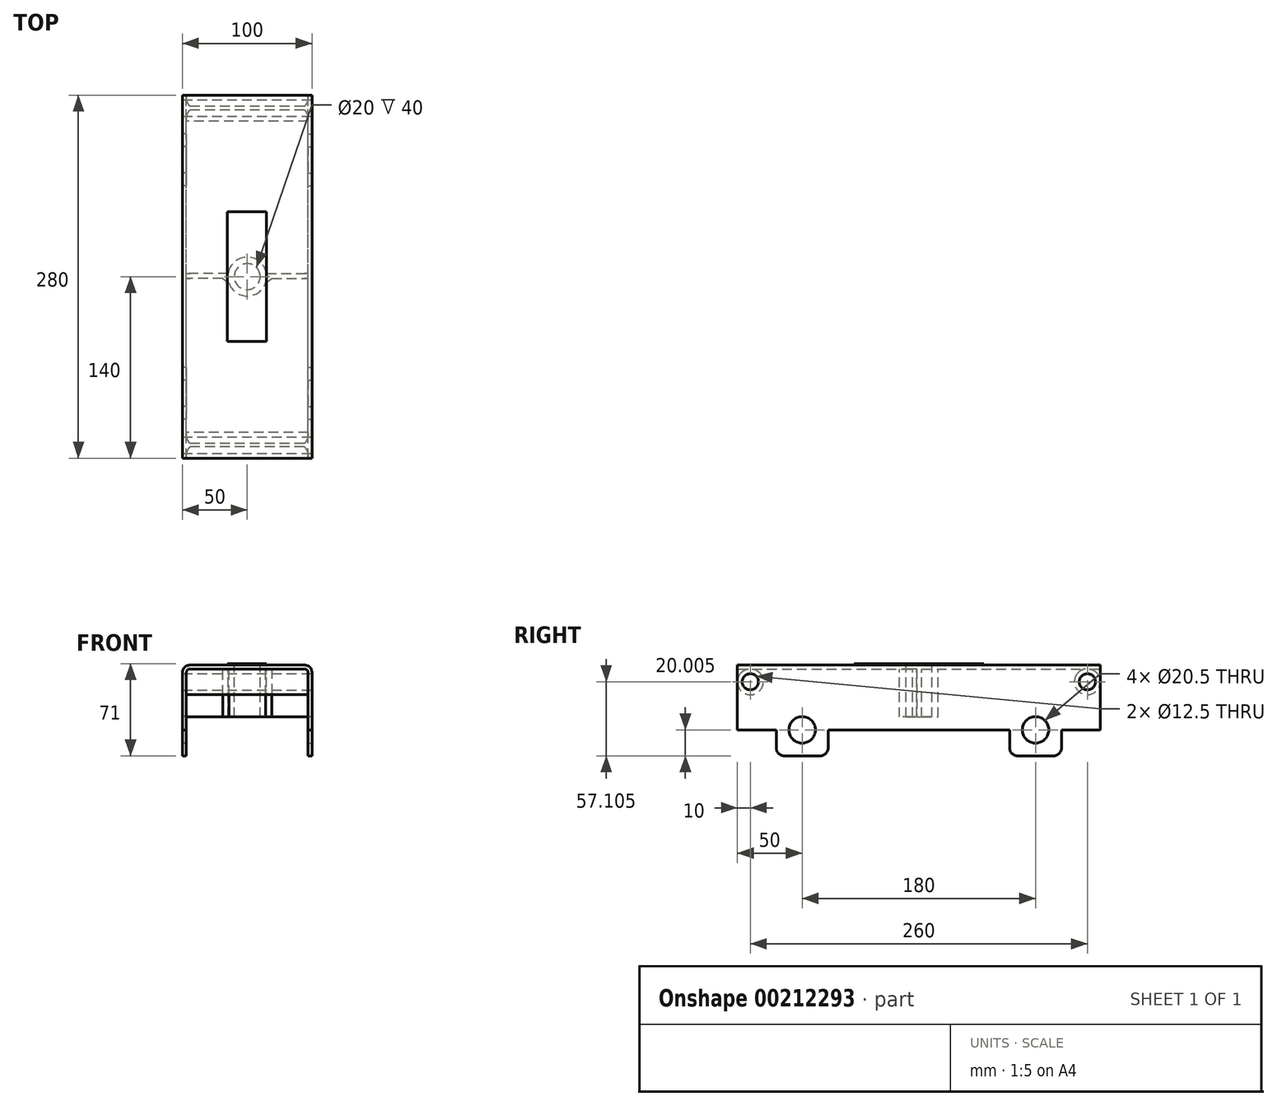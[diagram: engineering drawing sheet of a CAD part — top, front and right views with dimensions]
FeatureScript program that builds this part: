
annotation { "Feature Type Name" : "Feature", "Feature Type Description" : "" }
export const myFeature = defineFeature(function(context is Context, id is Id, definition is map)
    precondition{}
    {
        {
            var Q0;
            Q0=qCreatedBy(makeId("Front.planeOp"),FACE);
            var sketch = newSketch(context, id + "F0", { "sketchPlane" : qUnion([Q0])});
            skLineSegment(sketch, "E0", {"start": v(0, 20.85) * mm, "end": v(44, 20.85) * mm});
            skLineSegment(sketch, "E1", {"start": v(47, 17.85) * mm, "end": v(47, -26.15) * mm});
            skLineSegment(sketch, "E2", {"start": v(47, -26.15) * mm, "end": v(50, -26.15) * mm});
            skLineSegment(sketch, "E3", {"start": v(50, -26.15) * mm, "end": v(50, 17.85) * mm});
            skLineSegment(sketch, "E4", {"start": v(44, 23.85) * mm, "end": v(0, 23.85) * mm});
            skLineSegment(sketch, "E5", {"start": v(0, 20.85) * mm, "end": v(0, 23.85) * mm});
            skPoint(sketch, "E6.visualSharp", {"position": v(47, 20.85) * mm});
            skArc(sketch, "E6.filletArc", {"start": v(47, 17.85) * mm, "mid": v(46.12, 19.98) * mm, "end": v(44, 20.85) * mm});
            skPoint(sketch, "E7.visualSharp", {"position": v(50, 23.85) * mm});
            skArc(sketch, "E7.filletArc", {"start": v(50, 17.85) * mm, "mid": v(48.24, 22.1) * mm, "end": v(44, 23.85) * mm});
            skLineSegment(sketch, "E8.MirrorCS", {"start": v(-47, -26.15) * mm, "end": v(-50, -26.15) * mm});
            skArc(sketch, "E9.MirrorCS", {"start": v(-47, 17.85) * mm, "mid": v(-46.12, 19.98) * mm, "end": v(-44, 20.85) * mm});
            skLineSegment(sketch, "E10.MirrorCS", {"start": v(0, 20.85) * mm, "end": v(-44, 20.85) * mm});
            skLineSegment(sketch, "E11.MirrorCS", {"start": v(-47, 17.85) * mm, "end": v(-47, -26.15) * mm});
            skLineSegment(sketch, "E12.MirrorCS", {"start": v(-44, 23.85) * mm, "end": v(0, 23.85) * mm});
            skPoint(sketch, "E13.MirrorP", {"position": v(-47, 20.85) * mm});
            skPoint(sketch, "E14.MirrorP", {"position": v(-50, 23.85) * mm});
            skArc(sketch, "E15.MirrorCS", {"start": v(-50, 17.85) * mm, "mid": v(-48.24, 22.1) * mm, "end": v(-44, 23.85) * mm});
            skLineSegment(sketch, "E16.MirrorCS", {"start": v(-50, -26.15) * mm, "end": v(-50, 17.85) * mm});
            skSolve(sketch);
        }
        {
            var Q0;
            Q0=makeQuery(id+"F0.imprint","IMPRINT",FACE,{"disambiguationData":[TD([[makeQuery(id+"F0.imprint","IMPRINT",EDGE,{"derivedFrom":sQuery(id+"F0.wireOp",EDGE,"E0")}),1.0]])]});
            var Q1;
            Q1=makeQuery(id+"F0.imprint","IMPRINT",FACE,{"disambiguationData":[TD([[makeQuery(id+"F0.imprint","IMPRINT",EDGE,{"derivedFrom":sQuery(id+"F0.wireOp",EDGE,"E5")}),1.0]])]});
            extrude(context, id + "F1", {"entities" : qUnion([Q0, Q1]), "depth" : 280 * mm});
        }
        {
            var Q0;
            Q0=makeQuery(id+"F1.opExtrude","SWEPT_FACE",FACE,{"disambiguationData":[OSD([sQuery(id+"F0.wireOp",EDGE,"E3")])]});
            var sketch = newSketch(context, id + "F2", { "sketchPlane" : qUnion([Q0])});
            skLineSegment(sketch, "E17.bottom", {"start": v(-250, -26.15) * mm, "end": v(-210, -26.15) * mm});
            skLineSegment(sketch, "E17.top", {"start": v(-244, -46.15) * mm, "end": v(-216, -46.15) * mm});
            skLineSegment(sketch, "E17.left", {"start": v(-250, -26.15) * mm, "end": v(-250, -40.15) * mm});
            skLineSegment(sketch, "E17.right", {"start": v(-210, -26.15) * mm, "end": v(-210, -40.15) * mm});
            skLineSegment(sketch, "E18.bottom", {"start": v(-70, -26.15) * mm, "end": v(-30, -26.15) * mm});
            skLineSegment(sketch, "E18.top", {"start": v(-64, -46.15) * mm, "end": v(-36, -46.15) * mm});
            skLineSegment(sketch, "E18.left", {"start": v(-70, -26.15) * mm, "end": v(-70, -40.15) * mm});
            skLineSegment(sketch, "E18.right", {"start": v(-30, -26.15) * mm, "end": v(-30, -40.15) * mm});
            skPoint(sketch, "E19.visualSharp", {"position": v(-250, -46.15) * mm});
            skArc(sketch, "E19.filletArc", {"start": v(-250, -40.15) * mm, "mid": v(-248.24, -44.39) * mm, "end": v(-244, -46.15) * mm});
            skPoint(sketch, "E20.visualSharp", {"position": v(-210, -46.15) * mm});
            skArc(sketch, "E20.filletArc", {"start": v(-216, -46.15) * mm, "mid": v(-211.76, -44.39) * mm, "end": v(-210, -40.15) * mm});
            skPoint(sketch, "E21.visualSharp", {"position": v(-70, -46.15) * mm});
            skArc(sketch, "E21.filletArc", {"start": v(-70, -40.15) * mm, "mid": v(-68.24, -44.39) * mm, "end": v(-64, -46.15) * mm});
            skPoint(sketch, "E22.visualSharp", {"position": v(-30, -46.15) * mm});
            skArc(sketch, "E22.filletArc", {"start": v(-36, -46.15) * mm, "mid": v(-31.76, -44.39) * mm, "end": v(-30, -40.15) * mm});
            skCircle(sketch, "E23", {"center": v(-230, -26.15) * mm, "radius": 10.25 * mm});
            skCircle(sketch, "E24", {"center": v(-50, -26.15) * mm, "radius": 10.25 * mm});
            skSolve(sketch);
        }
        {
            var Q0;
            Q0=makeQuery(id+"F2.imprint","IMPRINT",FACE,{"disambiguationData":[TD([[makeQuery(id+"F2.imprint","IMPRINT",EDGE,{"derivedFrom":sQuery(id+"F2.wireOp",EDGE,"E17.bottom")}),-1.0]])]});
            var Q1;
            Q1=makeQuery(id+"F2.imprint","IMPRINT",FACE,{"disambiguationData":[TD([[makeQuery(id+"F2.imprint","IMPRINT",EDGE,{"derivedFrom":sQuery(id+"F2.wireOp",EDGE,"E18.bottom")}),-1.0]])]});
            extrude(context, id + "F3", {"entities" : qUnion([Q0, Q1]), "operationType" : NewBodyOperationType.ADD, "oppositeDirection" : true, "depth" : 3 * mm});
        }
        {
            var Q0;
            Q0=makeQuery(id+"F3.boolean.opBoolean","MERGE",FACE,{"derivedFrom":[makeQuery(id+"F1.opExtrude","SWEPT_FACE",FACE,{"disambiguationData":[OSD([sQuery(id+"F0.wireOp",EDGE,"E3")])]}),makeQuery(id+"F3.opExtrude","CAP_FACE",FACE,{"disambiguationData":[OSD([sQuery(id+"F2.wireOp",EDGE,"E17.bottom"),sQuery(id+"F2.wireOp",EDGE,"E17.top"),sQuery(id+"F2.wireOp",EDGE,"E17.left"),sQuery(id+"F2.wireOp",EDGE,"E17.right"),sQuery(id+"F2.wireOp",EDGE,"E19.filletArc"),sQuery(id+"F2.wireOp",EDGE,"E20.filletArc"),sQuery(id+"F2.wireOp",EDGE,"E23")])],"isStart":true}),makeQuery(id+"F3.opExtrude","CAP_FACE",FACE,{"disambiguationData":[OSD([sQuery(id+"F2.wireOp",EDGE,"E18.bottom"),sQuery(id+"F2.wireOp",EDGE,"E18.top"),sQuery(id+"F2.wireOp",EDGE,"E18.left"),sQuery(id+"F2.wireOp",EDGE,"E18.right"),sQuery(id+"F2.wireOp",EDGE,"E21.filletArc"),sQuery(id+"F2.wireOp",EDGE,"E22.filletArc"),sQuery(id+"F2.wireOp",EDGE,"E24")])],"isStart":true})]});
            var sketch = newSketch(context, id + "F4", { "sketchPlane" : qUnion([Q0])});
            skCircle(sketch, "E25", {"center": v(-230, -26.15) * mm, "radius": 10.25 * mm});
            skCircle(sketch, "E26", {"center": v(-50, -26.15) * mm, "radius": 10.25 * mm});
            skSolve(sketch);
        }
        {
            var Q0;
            {var subQ1=sQuery(id+"F2.wireOp",EDGE,"E23");var subQ2=sQuery(id+"F0.wireOp",EDGE,"E3");var subQ3=sQuery(id+"F0.wireOp",EDGE,"E2");var subQ4=makeQuery(id+"F3.boolean.opBoolean","SPLIT",EDGE,{"disambiguationData":[TD([makeQuery(id+"F3.opExtrude","SWEPT_FACE",FACE,{"disambiguationData":[OSD([subQ1])]})])],"derivedFrom":makeQuery(id+"F1.opExtrude","SWEPT_EDGE",EDGE,{"disambiguationData":[OSD([subQ3,subQ2])]})});Q0=makeQuery(id+"F4.imprint","IMPRINT",FACE,{"disambiguationData":[TD([[makeQuery(id+"F4.imprint","IMPRINT",EDGE,{"derivedFrom":subQ4}),1.0]])]});}
            var Q1;
            {var subQ1=sQuery(id+"F2.wireOp",EDGE,"E24");var subQ2=sQuery(id+"F0.wireOp",EDGE,"E3");var subQ3=sQuery(id+"F0.wireOp",EDGE,"E2");var subQ4=makeQuery(id+"F3.boolean.opBoolean","SPLIT",EDGE,{"disambiguationData":[TD([makeQuery(id+"F3.opExtrude","SWEPT_FACE",FACE,{"disambiguationData":[OSD([subQ1])]})])],"derivedFrom":makeQuery(id+"F1.opExtrude","SWEPT_EDGE",EDGE,{"disambiguationData":[OSD([subQ3,subQ2])]})});Q1=makeQuery(id+"F4.imprint","IMPRINT",FACE,{"disambiguationData":[TD([[makeQuery(id+"F4.imprint","IMPRINT",EDGE,{"derivedFrom":subQ4}),1.0]])]});}
            extrude(context, id + "F5", {"entities" : qUnion([Q0, Q1]), "operationType" : NewBodyOperationType.REMOVE, "oppositeDirection" : true, "depth" : 3 * mm});
        }
        {
            var Q0;
            Q0=makeQuery(id+"F1.opExtrude","SWEPT_FACE",FACE,{"disambiguationData":[OSD([sQuery(id+"F0.wireOp",EDGE,"E16.MirrorCS")])]});
            var sketch = newSketch(context, id + "F6", { "sketchPlane" : qUnion([Q0])});
            skLineSegment(sketch, "E27.bottom", {"start": v(30, -26.15) * mm, "end": v(70, -26.15) * mm});
            skLineSegment(sketch, "E27.top", {"start": v(36, -46.15) * mm, "end": v(64, -46.15) * mm});
            skLineSegment(sketch, "E27.left", {"start": v(30, -26.15) * mm, "end": v(30, -40.15) * mm});
            skLineSegment(sketch, "E27.right", {"start": v(70, -26.15) * mm, "end": v(70, -40.15) * mm});
            skLineSegment(sketch, "E28.bottom", {"start": v(210, -26.15) * mm, "end": v(250, -26.15) * mm});
            skLineSegment(sketch, "E28.top", {"start": v(216, -46.15) * mm, "end": v(244, -46.15) * mm});
            skLineSegment(sketch, "E28.left", {"start": v(210, -26.15) * mm, "end": v(210, -40.15) * mm});
            skLineSegment(sketch, "E28.right", {"start": v(250, -26.15) * mm, "end": v(250, -40.15) * mm});
            skCircle(sketch, "E29", {"center": v(50, -26.15) * mm, "radius": 10.25 * mm});
            skCircle(sketch, "E30", {"center": v(230, -26.15) * mm, "radius": 10.25 * mm});
            skPoint(sketch, "E31.visualSharp", {"position": v(30, -46.15) * mm});
            skArc(sketch, "E31.filletArc", {"start": v(30, -40.15) * mm, "mid": v(31.76, -44.39) * mm, "end": v(36, -46.15) * mm});
            skPoint(sketch, "E32.visualSharp", {"position": v(70, -46.15) * mm});
            skArc(sketch, "E32.filletArc", {"start": v(64, -46.15) * mm, "mid": v(68.24, -44.39) * mm, "end": v(70, -40.15) * mm});
            skPoint(sketch, "E33.visualSharp", {"position": v(210, -46.15) * mm});
            skArc(sketch, "E33.filletArc", {"start": v(210, -40.15) * mm, "mid": v(211.76, -44.39) * mm, "end": v(216, -46.15) * mm});
            skPoint(sketch, "E34.visualSharp", {"position": v(250, -46.15) * mm});
            skArc(sketch, "E34.filletArc", {"start": v(244, -46.15) * mm, "mid": v(248.24, -44.39) * mm, "end": v(250, -40.15) * mm});
            skSolve(sketch);
        }
        {
            var Q0;
            {var subQ0=sQuery(id+"F6.wireOp",EDGE,"E29");var subQ1=sQuery(id+"F6.wireOp",EDGE,"E27.bottom");var subQ2=makeQuery(id+"F6.imprint","INTERSECT",VERTEX,{"disambiguationData":[OD(0.0)],"derivedFrom":[subQ1,subQ0]});Q0=makeQuery(id+"F6.imprint","IMPRINT",FACE,{"disambiguationData":[TD([[makeQuery(id+"F6.imprint","IMPRINT",EDGE,{"disambiguationData":[TD([[subQ2,-1.0]])],"derivedFrom":subQ1}),-1.0]])]});}
            var Q1;
            {var subQ0=sQuery(id+"F6.wireOp",EDGE,"E30");var subQ1=sQuery(id+"F6.wireOp",EDGE,"E28.bottom");var subQ2=makeQuery(id+"F6.imprint","INTERSECT",VERTEX,{"disambiguationData":[OD(0.0)],"derivedFrom":[subQ1,subQ0]});Q1=makeQuery(id+"F6.imprint","IMPRINT",FACE,{"disambiguationData":[TD([[makeQuery(id+"F6.imprint","IMPRINT",EDGE,{"disambiguationData":[TD([[subQ2,-1.0]])],"derivedFrom":subQ1}),-1.0]])]});}
            extrude(context, id + "F7", {"entities" : qUnion([Q0, Q1]), "operationType" : NewBodyOperationType.REMOVE, "oppositeDirection" : true, "depth" : 3 * mm});
        }
        {
            var Q0;
            Q0=makeQuery(id+"F6.imprint","IMPRINT",FACE,{"disambiguationData":[TD([[makeQuery(id+"F6.imprint","IMPRINT",EDGE,{"derivedFrom":sQuery(id+"F6.wireOp",EDGE,"E27.top")}),1.0]])]});
            var Q1;
            Q1=makeQuery(id+"F6.imprint","IMPRINT",FACE,{"disambiguationData":[TD([[makeQuery(id+"F6.imprint","IMPRINT",EDGE,{"derivedFrom":sQuery(id+"F6.wireOp",EDGE,"E28.top")}),1.0]])]});
            extrude(context, id + "F8", {"entities" : qUnion([Q0, Q1]), "operationType" : NewBodyOperationType.ADD, "oppositeDirection" : true, "depth" : 3 * mm});
        }
        {
            var Q0;
            Q0=makeQuery(id+"F1.opExtrude","SWEPT_FACE",FACE,{"disambiguationData":[OSD([sQuery(id+"F0.wireOp",EDGE,"E4"),sQuery(id+"F0.wireOp",EDGE,"E12.MirrorCS")])]});
            var sketch = newSketch(context, id + "F9", { "sketchPlane" : qUnion([Q0])});
            skCircle(sketch, "E35", {"center": v(0, -140) * mm, "radius": 10 * mm});
            skSolve(sketch);
        }
        {
            var Q0;
            Q0 = qSketchRegion(id + "F9", true);
            extrude(context, id + "F10", {"entities" : qUnion([Q0]), "operationType" : NewBodyOperationType.REMOVE, "oppositeDirection" : true, "depth" : 3 * mm});
        }
        {
            var Q0;
            Q0=makeQuery(id+"F1.opExtrude","SWEPT_FACE",FACE,{"disambiguationData":[OSD([sQuery(id+"F0.wireOp",EDGE,"E0"),sQuery(id+"F0.wireOp",EDGE,"E10.MirrorCS")])]});
            var sketch = newSketch(context, id + "F11", { "sketchPlane" : qUnion([Q0])});
            skCircle(sketch, "E36", {"center": v(0, 140) * mm, "radius": 10 * mm});
            skCircle(sketch, "E37", {"center": v(0, 140) * mm, "radius": 15 * mm});
            skSolve(sketch);
        }
        {
            var Q0;
            Q0 = qSketchRegion(id + "F11", true);
            extrude(context, id + "F12", {"entities" : qUnion([Q0]), "operationType" : NewBodyOperationType.ADD, "depth" : 37 * mm});
        }
        {
            var Q0;
            Q0=makeQuery(id+"F1.opExtrude","SWEPT_FACE",FACE,{"disambiguationData":[OSD([sQuery(id+"F0.wireOp",EDGE,"E0"),sQuery(id+"F0.wireOp",EDGE,"E10.MirrorCS")])]});
            var sketch = newSketch(context, id + "F13", { "sketchPlane" : qUnion([Q0])});
            skLineSegment(sketch, "E38.left", {"start": v(14.83, 141.5) * mm, "end": v(14.83, 137.73) * mm});
            skLineSegment(sketch, "E39", {"start": v(14.83, 137.73) * mm, "end": v(47.07, 137.73) * mm});
            skLineSegment(sketch, "E40", {"start": v(14.83, 141.5) * mm, "end": v(47.07, 141.5) * mm});
            skLineSegment(sketch, "E41", {"start": v(47.07, 141.5) * mm, "end": v(47.07, 137.73) * mm});
            skLineSegment(sketch, "E42.MirrorCS", {"start": v(-14.83, 141.5) * mm, "end": v(-14.83, 137.73) * mm});
            skLineSegment(sketch, "E43.MirrorCS", {"start": v(-47.07, 141.5) * mm, "end": v(-47.07, 137.73) * mm});
            skLineSegment(sketch, "E44.MirrorCS", {"start": v(-14.83, 137.73) * mm, "end": v(-47.07, 137.73) * mm});
            skLineSegment(sketch, "E45.MirrorCS", {"start": v(-14.83, 141.5) * mm, "end": v(-47.07, 141.5) * mm});
            skSolve(sketch);
        }
        {
            var Q0;
            Q0=qCreatedBy(makeId("Right.planeOp"),FACE);
            var sketch = newSketch(context, id + "F14", { "sketchPlane" : qUnion([Q0])});
            skCircle(sketch, "E46", {"center": v(-270, 10.95) * mm, "radius": 10 * mm});
            skCircle(sketch, "E47", {"center": v(-10, 10.95) * mm, "radius": 10 * mm});
            skSolve(sketch);
        }
        {
            var Q0;
            Q0 = qSketchRegion(id + "F14", true);
            extrude(context, id + "F15", {"entities" : qUnion([Q0]), "operationType" : NewBodyOperationType.ADD, "depth" : 96 * mm, "symmetric" : true});
        }
        {
            var Q0;
            Q0 = qSketchRegion(id + "F13", true);
            extrude(context, id + "F16", {"entities" : qUnion([Q0]), "operationType" : NewBodyOperationType.ADD, "depth" : 37 * mm});
        }
        {
            var Q0;
            Q0=makeQuery(id+"F3.boolean.opBoolean","MERGE",FACE,{"derivedFrom":[makeQuery(id+"F1.opExtrude","SWEPT_FACE",FACE,{"disambiguationData":[OSD([sQuery(id+"F0.wireOp",EDGE,"E3")])]}),makeQuery(id+"F3.opExtrude","CAP_FACE",FACE,{"disambiguationData":[OSD([sQuery(id+"F2.wireOp",EDGE,"E17.bottom"),sQuery(id+"F2.wireOp",EDGE,"E17.top"),sQuery(id+"F2.wireOp",EDGE,"E17.left"),sQuery(id+"F2.wireOp",EDGE,"E17.right"),sQuery(id+"F2.wireOp",EDGE,"E19.filletArc"),sQuery(id+"F2.wireOp",EDGE,"E20.filletArc"),sQuery(id+"F2.wireOp",EDGE,"E23")])],"isStart":true}),makeQuery(id+"F3.opExtrude","CAP_FACE",FACE,{"disambiguationData":[OSD([sQuery(id+"F2.wireOp",EDGE,"E18.bottom"),sQuery(id+"F2.wireOp",EDGE,"E18.top"),sQuery(id+"F2.wireOp",EDGE,"E18.left"),sQuery(id+"F2.wireOp",EDGE,"E18.right"),sQuery(id+"F2.wireOp",EDGE,"E21.filletArc"),sQuery(id+"F2.wireOp",EDGE,"E22.filletArc"),sQuery(id+"F2.wireOp",EDGE,"E24")])],"isStart":true})]});
            var sketch = newSketch(context, id + "F17", { "sketchPlane" : qUnion([Q0])});
            skCircle(sketch, "E48", {"center": v(-270, 10.95) * mm, "radius": 6.25 * mm});
            skCircle(sketch, "E49", {"center": v(-10, 10.95) * mm, "radius": 6.25 * mm});
            skSolve(sketch);
        }
        {
            var Q0;
            Q0 = qSketchRegion(id + "F17", true);
            extrude(context, id + "F18", {"entities" : qUnion([Q0]), "operationType" : NewBodyOperationType.REMOVE, "endBound" : BoundingType.THROUGH_ALL, "oppositeDirection" : true, "depth" : 100 * mm});
        }
        {
            var Q0;
            Q0=makeQuery(id+"F1.opExtrude","SWEPT_FACE",FACE,{"disambiguationData":[OSD([sQuery(id+"F0.wireOp",EDGE,"E4"),sQuery(id+"F0.wireOp",EDGE,"E12.MirrorCS")])]});
            var sketch = newSketch(context, id + "F19", { "sketchPlane" : qUnion([Q0])});
            skLineSegment(sketch, "E50.bottom", {"start": v(-15.35, -90) * mm, "end": v(14.65, -90) * mm});
            skLineSegment(sketch, "E50.top", {"start": v(-15.35, -190) * mm, "end": v(14.65, -190) * mm});
            skLineSegment(sketch, "E50.left", {"start": v(-15.35, -90) * mm, "end": v(-15.35, -190) * mm});
            skLineSegment(sketch, "E50.right", {"start": v(14.65, -90) * mm, "end": v(14.65, -190) * mm});
            skSolve(sketch);
        }
        {
            var Q0;
            Q0 = qSketchRegion(id + "F19", true);
            extrude(context, id + "F20", {"entities" : qUnion([Q0]), "operationType" : NewBodyOperationType.ADD, "depth" : 1 * mm});
        }
        {
            var Q0;
            Q0=makeQuery(id+"F16.boolean.opBoolean","INTERSECT",EDGE,{"derivedFrom":[makeQuery(id+"F12.opExtrude","SWEPT_FACE",FACE,{"disambiguationData":[OSD([sQuery(id+"F11.wireOp",EDGE,"E37")])]}),makeQuery(id+"F16.opExtrude","SWEPT_FACE",FACE,{"disambiguationData":[OSD([sQuery(id+"F13.wireOp",EDGE,"E45.MirrorCS")])]})]});
            var Q1;
            Q1=makeQuery(id+"F16.opExtrude","SWEPT_EDGE",EDGE,{"disambiguationData":[OSD([sQuery(id+"F11.wireOp",EDGE,"E37"),sQuery(id+"F13.wireOp",EDGE,"E42.MirrorCS"),sQuery(id+"F13.wireOp",EDGE,"E44.MirrorCS")])]});
            var Q2;
            Q2=makeQuery(id+"F16.opExtrude","SWEPT_EDGE",EDGE,{"disambiguationData":[OSD([sQuery(id+"F11.wireOp",EDGE,"E37"),sQuery(id+"F13.wireOp",EDGE,"E38.left"),sQuery(id+"F13.wireOp",EDGE,"E39")])]});
            var Q3;
            Q3=makeQuery(id+"F16.boolean.opBoolean","INTERSECT",EDGE,{"derivedFrom":[makeQuery(id+"F12.opExtrude","SWEPT_FACE",FACE,{"disambiguationData":[OSD([sQuery(id+"F11.wireOp",EDGE,"E37")])]}),makeQuery(id+"F16.opExtrude","SWEPT_FACE",FACE,{"disambiguationData":[OSD([sQuery(id+"F13.wireOp",EDGE,"E40")])]})]});
            chamfer(context, id + "F21", {"entities" : qUnion([Q0, Q1, Q2, Q3]), "width" : 5 * mm, "tangentPropagation" : true});
        }
    });
